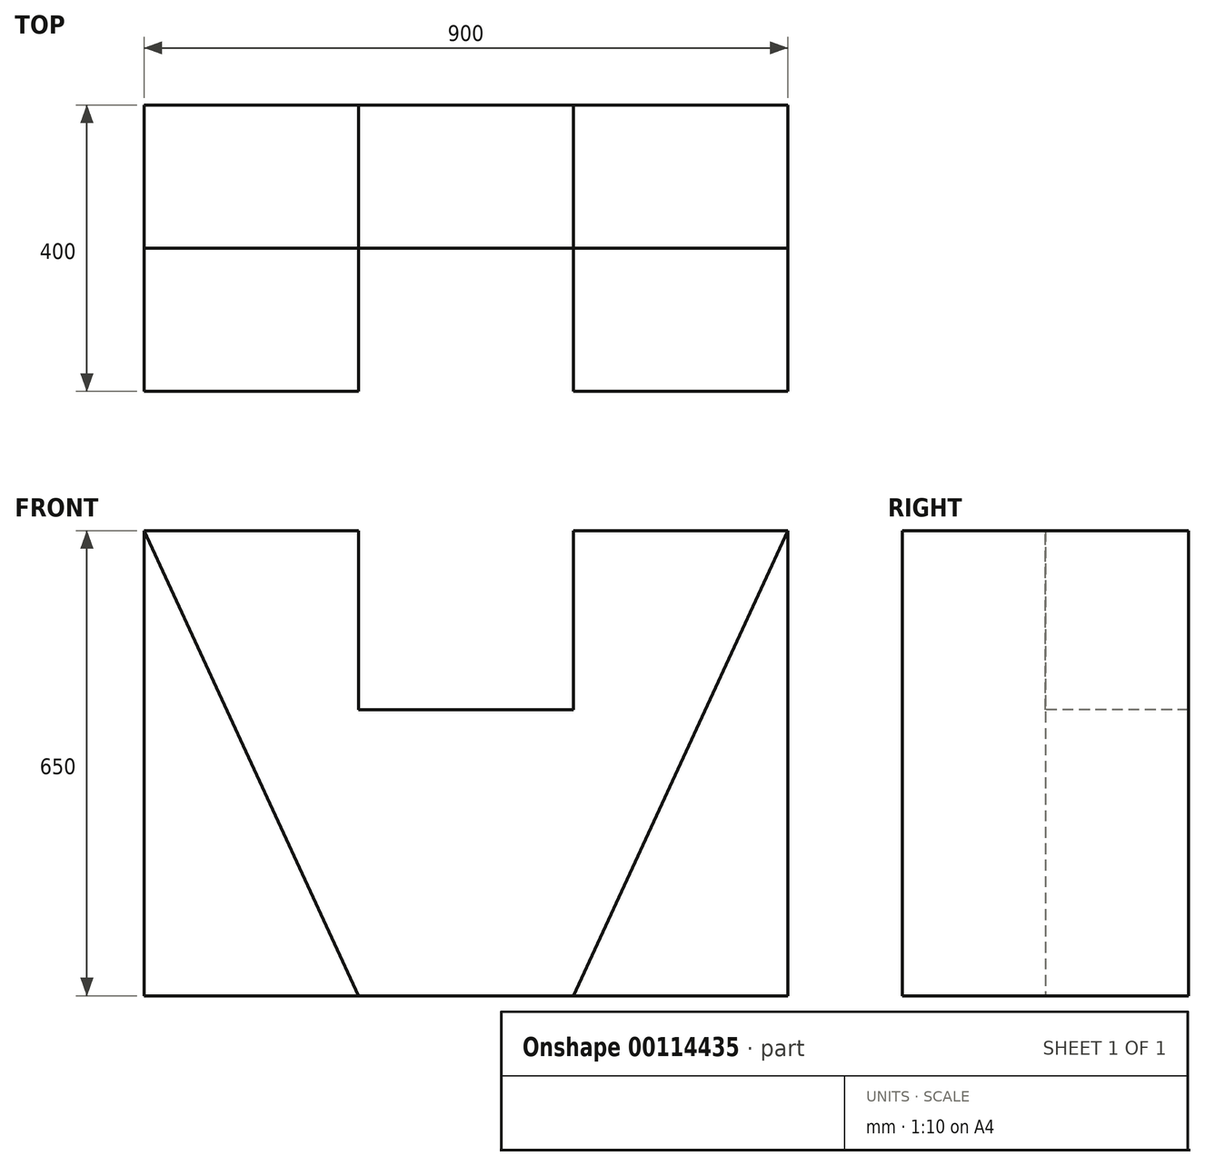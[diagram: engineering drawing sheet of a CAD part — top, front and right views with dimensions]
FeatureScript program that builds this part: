
annotation { "Feature Type Name" : "Feature", "Feature Type Description" : "" }
export const myFeature = defineFeature(function(context is Context, id is Id, definition is map)
    precondition{}
    {
        {
            var Q0;
            Q0=qCreatedBy(makeId("Front.planeOp"),FACE);
            var sketch = newSketch(context, id + "F0", { "sketchPlane" : qUnion([Q0])});
            skLineSegment(sketch, "E0.bottom", {"start": v(450, -325) * mm, "end": v(-450, -325) * mm});
            skLineSegment(sketch, "E0.top", {"start": v(450, 325) * mm, "end": v(-450, 325) * mm});
            skLineSegment(sketch, "E0.left", {"start": v(450, -325) * mm, "end": v(450, 325) * mm});
            skLineSegment(sketch, "E0.right", {"start": v(-450, -325) * mm, "end": v(-450, 325) * mm});
            skPoint(sketch, "E0.middle", {"position": v(0, 0) * mm});
            skSolve(sketch);
        }
        {
            var Q0;
            Q0 = qSketchRegion(id + "F0", true);
            extrude(context, id + "F1", {"entities" : qUnion([Q0]), "depth" : 400 * mm});
        }
        {
            var Q0;
            Q0=makeQuery(id+"F1.opExtrude","CAP_FACE",FACE,{"disambiguationData":[OSD([sQuery(id+"F0.wireOp",EDGE,"E0.bottom"),sQuery(id+"F0.wireOp",EDGE,"E0.top"),sQuery(id+"F0.wireOp",EDGE,"E0.left"),sQuery(id+"F0.wireOp",EDGE,"E0.right")])],"isStart":false});
            var sketch = newSketch(context, id + "F2", { "sketchPlane" : qUnion([Q0])});
            skLineSegment(sketch, "E1", {"start": v(-450, 325) * mm, "end": v(-150, -325) * mm});
            skLineSegment(sketch, "E2", {"start": v(-150, -325) * mm, "end": v(150, -325) * mm});
            skLineSegment(sketch, "E3", {"start": v(150, -325) * mm, "end": v(450, 325) * mm});
            skLineSegment(sketch, "E4", {"start": v(450, 325) * mm, "end": v(-450, 325) * mm});
            skSolve(sketch);
        }
        {
            var Q0;
            Q0=makeQuery(id+"F2.imprint","IMPRINT",FACE,{"disambiguationData":[TD([[makeQuery(id+"F2.imprint","IMPRINT",EDGE,{"derivedFrom":sQuery(id+"F2.wireOp",EDGE,"E1")}),1.0]])]});
            extrude(context, id + "F3", {"entities" : qUnion([Q0]), "operationType" : NewBodyOperationType.REMOVE, "oppositeDirection" : true, "depth" : 200 * mm});
        }
        {
            var Q0;
            Q0=makeQuery(id+"F3.boolean.opBoolean","COPY",FACE,{"derivedFrom":makeQuery(id+"F3.opExtrude","CAP_FACE",FACE,{"disambiguationData":[OSD([sQuery(id+"F2.wireOp",EDGE,"E1"),sQuery(id+"F2.wireOp",EDGE,"E2"),sQuery(id+"F2.wireOp",EDGE,"E3"),sQuery(id+"F2.wireOp",EDGE,"E4")])],"isStart":false})});
            var sketch = newSketch(context, id + "F4", { "sketchPlane" : qUnion([Q0])});
            skLineSegment(sketch, "E5.bottom", {"start": v(-150, 75) * mm, "end": v(150, 75) * mm});
            skLineSegment(sketch, "E5.top", {"start": v(-150, 575) * mm, "end": v(150, 575) * mm});
            skLineSegment(sketch, "E5.left", {"start": v(-150, 75) * mm, "end": v(-150, 575) * mm});
            skLineSegment(sketch, "E5.right", {"start": v(150, 75) * mm, "end": v(150, 575) * mm});
            skPoint(sketch, "E5.middle", {"position": v(0, 325) * mm});
            skSolve(sketch);
        }
        {
            var Q0;
            Q0 = qSketchRegion(id + "F4", true);
            extrude(context, id + "F5", {"entities" : qUnion([Q0]), "operationType" : NewBodyOperationType.REMOVE, "oppositeDirection" : true, "depth" : 250 * mm});
        }
    });
